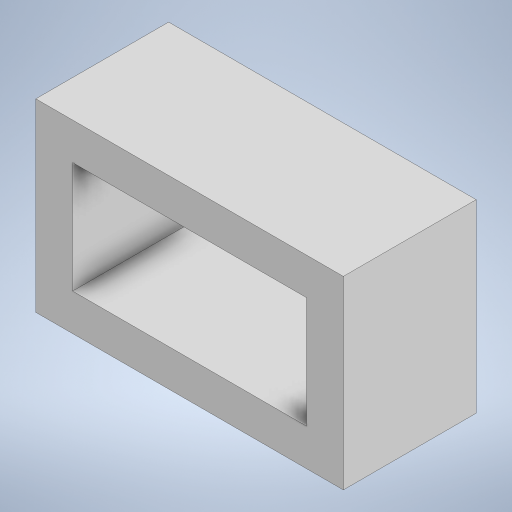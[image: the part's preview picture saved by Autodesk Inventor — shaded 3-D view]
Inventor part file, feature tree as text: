
AUTODESK INVENTOR PART (.ipt)
format: ipt  version: 2023 (Build 270158000, 158)  size: 573,952 bytes
history: native  units: mm
features: other x3, extrude x1, sketch x1
ambient origin geometry x8: Origin, YZ Plane, XZ Plane, XY Plane, X Axis, Y Axis, Z Axis, Center Point
bodies: Solid2 (feature_tree), Solid1 (feature_tree)
feature tree (5):
  other  "JST - XH - Thru (V) - 4Pin - 2.54mm.ipt"
  extrude  "Extrusion1"  Depth=0.1mm
  other  "Solid1::JST - XH - Thru (V) - 4Pin - 2.54mm.ipt"
  other  "TaggingFeature1"
  sketch  "Sketch1"  dims[d0=10.0mm d1=0.1mm d2=2.0mm d3=7.0mm d4=0.0mm d5=12.7mm d6=6.042mm]
